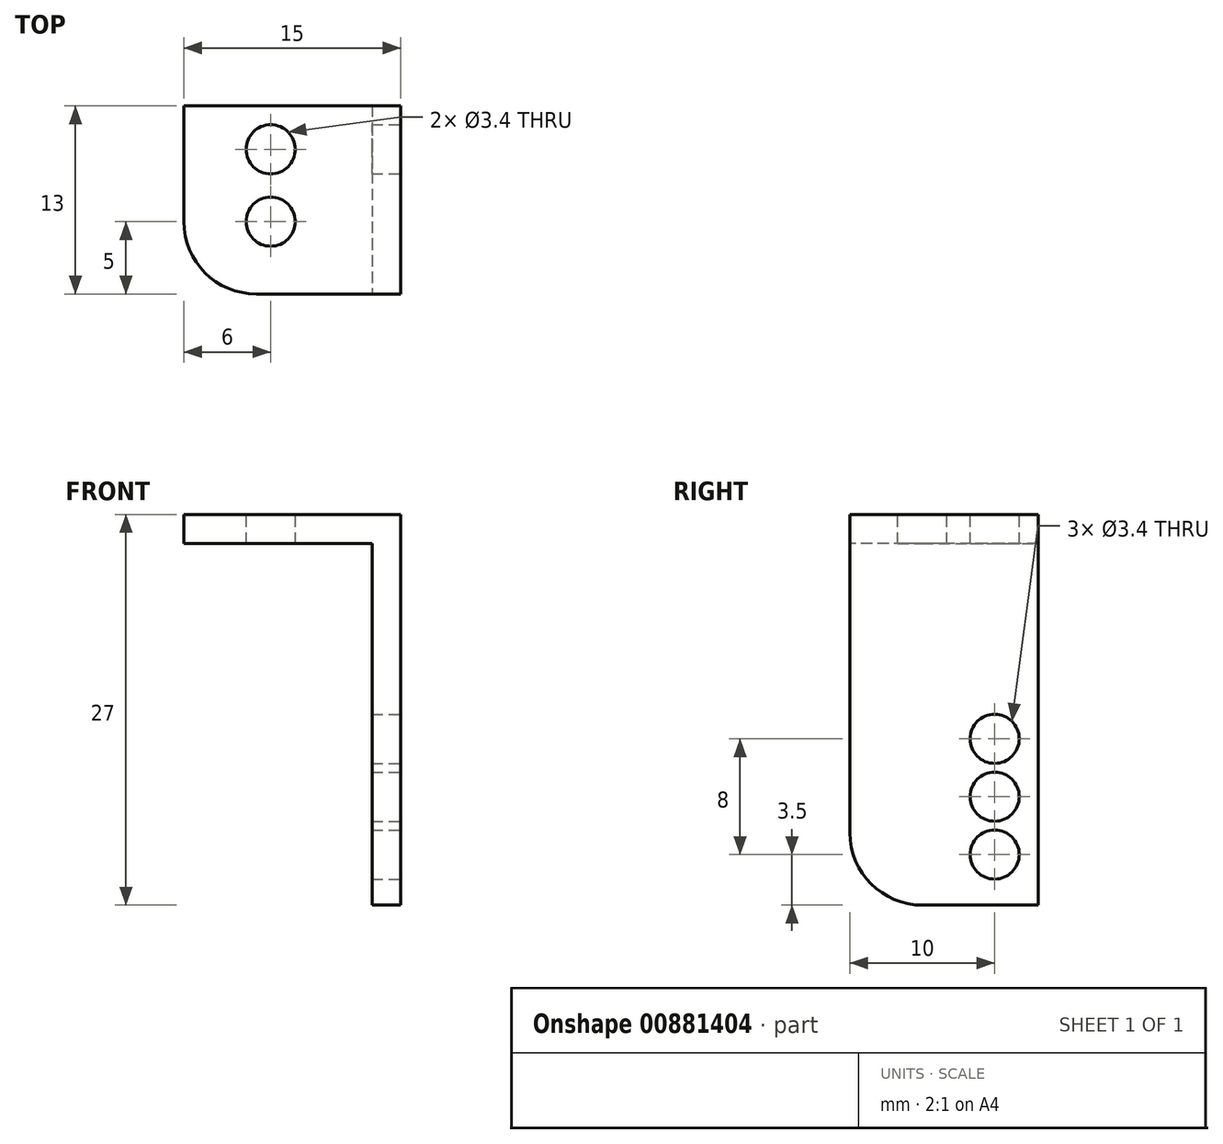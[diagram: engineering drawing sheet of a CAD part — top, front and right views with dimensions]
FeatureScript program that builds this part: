
annotation { "Feature Type Name" : "Feature", "Feature Type Description" : "" }
export const myFeature = defineFeature(function(context is Context, id is Id, definition is map)
    precondition{}
    {
        {
            var Q0;
            Q0=qCreatedBy(makeId("Top.planeOp"),FACE);
            var sketch = newSketch(context, id + "F0", { "sketchPlane" : qUnion([Q0])});
            skLineSegment(sketch, "E0.bottom", {"start": v(7.5, -10) * mm, "end": v(-7.5, -10) * mm});
            skLineSegment(sketch, "E0.top", {"start": v(7.5, 10) * mm, "end": v(-7.5, 10) * mm});
            skLineSegment(sketch, "E0.left", {"start": v(7.5, -10) * mm, "end": v(7.5, 10) * mm});
            skLineSegment(sketch, "E0.right", {"start": v(-7.5, -10) * mm, "end": v(-7.5, 10) * mm});
            skPoint(sketch, "E0.middle", {"position": v(0, 0) * mm});
            skPoint(sketch, "E1", {"position": v(-1.5, 5) * mm});
            skPoint(sketch, "E2", {"position": v(-1.5, 0) * mm});
            skPoint(sketch, "E3", {"position": v(-1.5, -5) * mm});
            skPoint(sketch, "E4", {"position": v(5.5, 10) * mm});
            skPoint(sketch, "E5", {"position": v(5.5, -10) * mm});
            skLineSegment(sketch, "E6", {"start": v(5.5, 10) * mm, "end": v(5.5, -10) * mm});
            skSolve(sketch);
        }
        {
            var Q0;
            Q0=makeQuery(id+"F0.imprint","IMPRINT",FACE,{"disambiguationData":[TD([[makeQuery(id+"F0.imprint","IMPRINT",EDGE,{"derivedFrom":sQuery(id+"F0.wireOp",EDGE,"E0.bottom")}),-1.0]])]});
            extrude(context, id + "F1", {"entities" : qUnion([Q0]), "depth" : 2 * mm, "offsetDistance" : 25 * mm});
        }
        {
            var Q0;
            Q0=sQuery(id+"F0.wireOp",VERTEX,"E1");
            var Q1;
            Q1=sQuery(id+"F0.wireOp",VERTEX,"E2");
            var Q2;
            Q2=sQuery(id+"F0.wireOp",VERTEX,"E3");
            var Q3;
            Q3=makeQuery(id+"F1.opExtrude","SWEPT_BODY",BODY,{"disambiguationData":[OSD([sQuery(id+"F0.wireOp",EDGE,"E0.bottom"),sQuery(id+"F0.wireOp",EDGE,"E0.top"),sQuery(id+"F0.wireOp",EDGE,"E0.left"),sQuery(id+"F0.wireOp",EDGE,"E0.right")])]});
            hole(context, id + "F2", {"style" : HoleStyle.SIMPLE, "endStyle" : HoleEndStyle.THROUGH, "oppositeDirection" : true, "standardTappedOrClearance" : lookupTablePath({ "fit" : "Normal", "standard" : "ISO", "size" : "M3", "type" : "Clearance" }), "standardBlindInLast" : lookupTablePath({ "fit" : "Normal", "standard" : "ISO", "engagement" : "75%", "pitch" : "0.5 mm", "size" : "M3", "type" : "Clearance & tapped" }), "holeDiameter" : 3.4 * mm, "majorDiameter" : 5 * mm, "isTappedThrough" : true, "tappedDepth" : 12 * mm, "tapClearance" : 3, "locations" : qUnion([Q0, Q1, Q2]), "scope" : qUnion([Q3]), "startStyle" : HoleStartStyle.SKETCH});
        }
        {
            var Q0;
            {var subQ2=sQuery(id+"F0.wireOp",EDGE,"E0.left");Q0=makeQuery(id+"F0.imprint","IMPRINT",FACE,{"disambiguationData":[TD([[makeQuery(id+"F0.imprint","IMPRINT",EDGE,{"derivedFrom":subQ2}),1.0]])]});}
            extrude(context, id + "F3", {"entities" : qUnion([Q0]), "operationType" : NewBodyOperationType.ADD, "oppositeDirection" : true, "depth" : 25 * mm, "offsetDistance" : 25 * mm});
        }
        {
            var Q0;
            Q0=makeQuery(id+"F3.opExtrude","SWEPT_FACE",FACE,{"disambiguationData":[OSD([sQuery(id+"F0.wireOp",EDGE,"E6")])]});
            var sketch = newSketch(context, id + "F4", { "sketchPlane" : qUnion([Q0])});
            skPoint(sketch, "E7", {"position": v(0, -17.5) * mm});
            skPoint(sketch, "E8", {"position": v(0, -13.5) * mm});
            skPoint(sketch, "E9", {"position": v(0, -21.5) * mm});
            skSolve(sketch);
        }
        {
            var Q0;
            Q0=sQuery(id+"F4.wireOp",VERTEX,"E7");
            var Q1;
            Q1=sQuery(id+"F4.wireOp",VERTEX,"E8");
            var Q2;
            Q2=sQuery(id+"F4.wireOp",VERTEX,"E9");
            var Q3;
            Q3=makeQuery(id+"F1.opExtrude","SWEPT_BODY",BODY,{"disambiguationData":[OSD([sQuery(id+"F0.wireOp",EDGE,"E0.bottom"),sQuery(id+"F0.wireOp",EDGE,"E0.top"),sQuery(id+"F0.wireOp",EDGE,"E0.left"),sQuery(id+"F0.wireOp",EDGE,"E0.right")])]});
            hole(context, id + "F5", {"style" : HoleStyle.SIMPLE, "endStyle" : HoleEndStyle.THROUGH, "standardTappedOrClearance" : lookupTablePath({ "fit" : "Normal", "standard" : "ISO", "size" : "M3", "type" : "Clearance" }), "standardBlindInLast" : lookupTablePath({ "fit" : "Normal", "standard" : "ISO", "engagement" : "75%", "pitch" : "0.5 mm", "size" : "M3", "type" : "Clearance & tapped" }), "holeDiameter" : 3.4 * mm, "majorDiameter" : 5 * mm, "isTappedThrough" : true, "tappedDepth" : 12 * mm, "tapClearance" : 3, "locations" : qUnion([Q0, Q1, Q2]), "scope" : qUnion([Q3]), "startStyle" : HoleStartStyle.SKETCH});
        }
        {
            var Q0;
            {var subQ0=sQuery(id+"F0.wireOp",EDGE,"E0.top");Q0=makeQuery(id+"F3.boolean.opBoolean","MERGE",FACE,{"derivedFrom":[makeQuery(id+"F1.opExtrude","SWEPT_FACE",FACE,{"disambiguationData":[OSD([subQ0])]}),makeQuery(id+"F3.opExtrude","SWEPT_FACE",FACE,{"disambiguationData":[OSD([subQ0])]})]});}
            extrude(context, id + "F6", {"entities" : qUnion([Q0]), "operationType" : NewBodyOperationType.REMOVE, "oppositeDirection" : true, "depth" : 7 * mm, "offsetDistance" : 25 * mm});
        }
        {
            var Q0;
            {var subQ0=sQuery(id+"F0.wireOp",EDGE,"E0.top");Q0=makeQuery(id+"F6.boolean.opBoolean","COPY",EDGE,{"derivedFrom":makeQuery(id+"F6.opExtrude","CAP_EDGE",EDGE,{"disambiguationData":[OSD([subQ0]),TDD([makeQuery(id+"F3.opExtrude","CAP_EDGE",EDGE,{"disambiguationData":[OSD([subQ0])],"isStart":false})])],"isStart":false})});}
            var Q1;
            Q1=makeQuery(id+"F3.opExtrude","CAP_EDGE",EDGE,{"disambiguationData":[OSD([sQuery(id+"F0.wireOp",EDGE,"E0.bottom")])],"isStart":false});
            var Q2;
            Q2=makeQuery(id+"F1.opExtrude","SWEPT_EDGE",EDGE,{"disambiguationData":[OSD([sQuery(id+"F0.wireOp",EDGE,"E0.bottom"),sQuery(id+"F0.wireOp",EDGE,"E0.right")])]});
            var Q3;
            Q3=makeQuery(id+"F6.boolean.opBoolean","COPY",EDGE,{"derivedFrom":makeQuery(id+"F6.opExtrude","CAP_EDGE",EDGE,{"disambiguationData":[OSD([sQuery(id+"F0.wireOp",EDGE,"E0.top"),sQuery(id+"F0.wireOp",EDGE,"E0.right")])],"isStart":false})});
            fillet(context, id + "F7", {"entities" : qUnion([Q0, Q1, Q2, Q3]), "tangentPropagation" : true, "radius" : 5 * mm, "defaultsChanged" : false, "vertexSettings" : [], "allowEdgeOverflow" : false});
        }
    });
